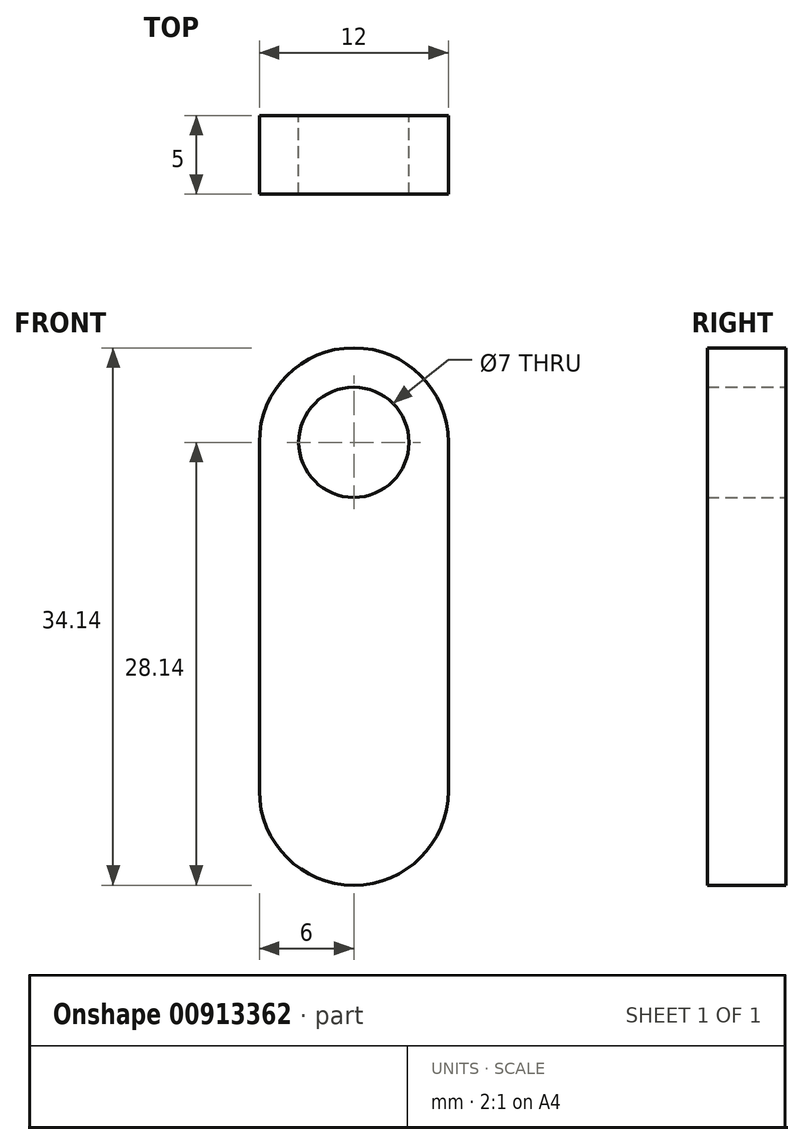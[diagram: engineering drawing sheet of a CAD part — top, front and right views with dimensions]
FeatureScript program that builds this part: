
annotation { "Feature Type Name" : "Feature", "Feature Type Description" : "" }
export const myFeature = defineFeature(function(context is Context, id is Id, definition is map)
    precondition{}
    {
        {
            var Q0;
            Q0=qCreatedBy(makeId("Front.planeOp"),FACE);
            var sketch = newSketch(context, id + "F0", { "sketchPlane" : qUnion([Q0])});
            skCircle(sketch, "E0", {"center": v(0, 0) * mm, "radius": 3.5 * mm});
            skArc(sketch, "E1", {"start": v(6, 0) * mm, "mid": v(0, 6) * mm, "end": v(-6, 0) * mm});
            skArc(sketch, "E2", {"start": v(-6, -22.14) * mm, "mid": v(0, -28.14) * mm, "end": v(6, -22.14) * mm});
            skLineSegment(sketch, "E3", {"start": v(-6, -22.14) * mm, "end": v(-6, 0) * mm});
            skLineSegment(sketch, "E4.MirrorCS", {"start": v(6, -22.14) * mm, "end": v(6, 0) * mm});
            skSolve(sketch);
        }
        {
            var Q0;
            Q0 = qSketchRegion(id + "F0", true);
            extrude(context, id + "F1", {"entities" : qUnion([Q0]), "depth" : 5 * mm, "offsetDistance" : 25 * mm});
        }
    });
